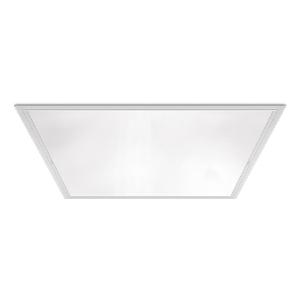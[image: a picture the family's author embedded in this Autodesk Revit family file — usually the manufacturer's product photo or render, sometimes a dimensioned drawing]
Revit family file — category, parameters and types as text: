
# Revit family: 3f_filippi_-_l_600_luce_diffusa_lgs_3f_filippi_-_22840_-_l_600_52w-940_dali_lgs_596x596
name_source: partatom
category: Lighting Fixtures
units: mm (PartAtom-declared; Revit-internal decimal feet)

## family parameters
Cut with Voids When Loaded = No
Host = Face
Light Source = No
Part Type = Normal
Room Calculation Point = No
Round Connector Dimension = Use Diameter
Shared = No

## types (1)
- 3F Filippi - L 600 Luce Diffusa LGS (1 x LED, 5843 lm, 55.5 W, 4000 K)
    Apparent Load = 56 VA
    Approval mark = ENEC
    CIE Flux Codes = 66 93 98 100 100
    Color Rendering = 90
    Color Temperature = 4000 K
    Control Gear = Electronic transformer
    Default Elevation = 1800 mm
    Description = ILLUMINOTECHNICAL
Luminous efficiency 100% (DLOR 100%, ULOR 0%).
Initial luminous flux of the luminaire 5843 lm.
Direct symmetric distribution.
Installation Interdistance Transv.D = 1.14 x hu - Long.D = 1.16 x hu.
Average luminance <3000 cd/m² for radial angles >65°.
Tabular UGR (CIE 117 - 4H-8H; S=0.25H; 70/50/20): RUG 17.9 - 17.9.
Beam angle: 85° - 85°.
Luminous efficacy 105 lm/W.
Lifetime (L93/B10): 30000 h. (tq+25°C)
Lifetime (L90/B10): 50000 h. (tq+25°C)
Lifetime (L85/B10): 80000 h. (tq+25°C)
Lifetime (L80/B10): 100000 h. (tq+25°C)
Sudden decreased luminous flux after 50000 hours: 0% (C0).
Photobiological safety in compliance with IEC/TR 62778: RG0 risk exempt, (IEC 62471).
In compliance with IEC/EN 62722-2-1 - IEC/EN 62717 standards.

SOURCE
Squared LED module 52W/940.
Source with special protection against aggressive chemically-volatile substances for standard LED technology.
Energy efficiency class (UE 2019/2020 - UE 2019/2015): E.
CIE 13.3 Colour rendering index: CRI >90 (R9 >50%).
IES TM-30 Fidelity Index: Rf = 92 Rg = 101.
CCT nominal colour temperature 4000 K.
Colour initial tolerance (MacAdam): SDCM 3.

MECHANICAL
Housing in galvannealed steel, painted in white epoxy-polyester.
Perimetral frame in white polycarbonate.
LGS micro-prismatic flat diffuser in transparent methacrylate (PMMA), multi-lenticular exterior, anti-glare.
Anti-glare opal polycarbonate filter for brightness uniformity.
Luminaire with limited surface temperature. - D - (EN 60598-2-24)
Dimensions: 596x596 mm, height 95 mm. Weight 5.345 kg.
IP65 protection degree for exposed part, IP64 for recessed part.
Mechanical strength to impacts IK06 (1 joule).
Glow-wire test resistance 650°C.

ELECTRICAL
Halogen Free DALI-2, PUSH-DIM, electronic wiring 230V-50/60Hz, power factor 0.95 at full load, THD <25%, constant output current, class I, 1 driver, 1 DALI addresse.
Power of the luminaire 55.5 W.
CE - IEC 60598-1 - EN 60598-1.
SAFE FLICKER: PstLM=<1 and SVM=<0.4 (IEC TR 61547-1 and IEC TR 63158), to ensure a more comfortable and safe light.
Luminaire compliant with EN 60598-2-22 for power supply from a centralised emergency system CPSS (Central Power Supply System), not incorporated in the luminaire - high risk areas excluded. The default power and flux are 100% in AC and 15% in DC.
Ambient temperature from 0°C to +40°C.
Temperature class T6 max 85°C.
5-pole terminal block (L-N-PE-DA/DA) quick connection for line connection with connection capacity 2x2.5 mm² per poles.
Relative humidity UR: <85%.

INSTALLATION
Lay-on or pull-up recessed fitting using frame accessory.
All accessories dedicated to this product are available on the Catalog and on our website www.3F-Filippi.com.

APPLICATIONS
Suitable product for food production plants (HACCP), IFS (Food Version 6), BRC (GSFS Food Version 7).
In environments requiring protection and simplified cleaning.
Hospitals, pharmaceutical, chemical, aseptic laboratories, sterilised rooms.
Environments with VDTs.
Environments where demanding visual tasks are performed and soft diffuse light is required for optimal visual comfort and total shielding of the light source.

LIGHT MANAGEMENT
Recommended minimum setting: 10%.
The device, equipped with DALI-2 driver, can be controlled manually with 3F Easy Dim technology or automatically/manually with 3F Smart Dimming technology and/or centralised DALI systems.
DALI-2 certification guarantees interoperability with other devices with the same certification.
In electrical systems without a regulation system (manual or automatic) and DALI bus, a suitable jumper must be made on the DA-DA terminals of the appliance.

WARNING
Luminaire designed for disposal/recycling at end-of-life.
Replaceable (LED only) light source by a professional. Replaceable control gear by a professional.
    Height = 0 mm  [stored 0 ft]
    Lamp = 1 x LED
    Lamp Light Flux = 5843 lm
    Lamp Power = 55.5 W
    Lamp count = 1
    Length = 596 mm
    Lifetime = 50000 h
    Luminous efficacy = 105 lm/W
    Manufacturer = 3F Filippi
    ModVariant = No
    Model = 3F Filippi - 22840 - L 600 52W-940 DALI LGS 596x596
    Mounting Place = Ceiling
    Mounting Type = Recessed
    Number of Poles = 1
    OnlyDefault = Yes
    Power Factor = 1
    Product Name = 3F Filippi - L 600 Luce Diffusa LGS
    Product group = recessed luminaire
    ProductGroupID = 4
    Protection Class = Protection class I
    Protection Degree = IP 64
    RLX_Detail_Level = 1
    RLX_Emergency_Light_Flux = 0 lm
    RLX_Emergency_Type = 0
    RLX_Emergency_Type_DB = No
    RlxData = <blob elided: 128641 chars, md5=3fc5b749>
    Socket = socket
    Standby Power = 0 W
    System Light Flux = 5843 lm
    System Power = 56 W
    Type Comments = Product without accessories
    Type Image = 3ffilippi_l_600_luce_diffusa_lgs.jpg
    URL = http://relux.com
    VarID = ---
    Voltage = 0 V
    Weight = 0.00 kg
    Width = 596 mm

note: [stored X ft] marks values corroborated as IEEE doubles in the binary element streams (Revit-internal decimal feet)

## geometry (parser evidence)
native form markers: Blend x4, Sweep x12
no freeform markers — native parametric forms only
